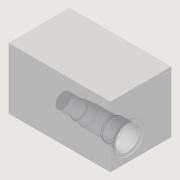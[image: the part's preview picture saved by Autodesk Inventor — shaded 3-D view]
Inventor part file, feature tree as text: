
AUTODESK INVENTOR PART (.ipt)
format: ipt  version: 2014 (Build 180170000, 170)  size: 204,800 bytes
history: native  units: mm
features: other x48, extrude x22, sketch x22
ambient origin geometry x8: Origin, YZ Plane, XZ Plane, XY Plane, X Axis, Y Axis, Z Axis, Center Point
bodies: 实体1 (feature_tree)
feature tree (92):
  extrude  "拉伸1"  Depth=30.2mm
  other  "UCS1"
  other  "UCS2"
  other  "UCS3"
  other  "UCS4"
  other  "UCS5"
  other  "UCS6"
  extrude  "拉伸2"  Depth=18.0mm
  extrude  "拉伸3"  Depth=0.79mm
  extrude  "拉伸5"  Depth=22.22mm
  extrude  "拉伸6"  Depth=14.28mm
  extrude  "拉伸7"  Depth=16.5mm TaperAngle=0.0deg
  extrude  "拉伸8"  Depth=38.5mm TaperAngle=0.0deg
  extrude  "拉伸9"  Depth=17.5mm
  extrude  "拉伸10"  Depth=47.63mm
  extrude  "拉伸11"  Depth=63.5mm TaperAngle=0.0deg
  extrude  "拉伸12"  Depth=63.5mm
  extrude  "拉伸13"  Depth=140.0mm
  extrude  "拉伸14"  Depth=0.79mm
  extrude  "拉伸15"  Depth=2.74mm
  extrude  "拉伸16"  Depth=12.7mm TaperAngle=0.0deg
  extrude  "拉伸17"  Depth=60.0mm TaperAngle=0.0deg
  extrude  "拉伸18"  Depth=60.0mm
  extrude  "拉伸19"  Depth=60.0mm
  extrude  "拉伸20"  Depth=60.0mm TaperAngle=0.0deg
  extrude  "拉伸21"  Depth=60.0mm
  extrude  "拉伸22"  Depth=60.0mm
  extrude  "拉伸23"  Depth=60.0mm TaperAngle=0.0deg
  sketch  "草图1"  dims[d0=60.0mm d1=0.0mm]
  sketch  "草图2"  dims[d2=0.0mm d3=0.0mm d4=0.0mm d5=0.0mm d6=0.0mm d7=0.0mm]
  sketch  "草图3"  dims[d8=0.0mm d9=0.0mm d10=0.0mm d11=0.0mm d12=0.0mm d13=0.0mm]
  sketch  "草图6"  dims[d14=0.0mm d15=0.0mm d16=0.0mm d17=0.0mm d18=0.0mm d19=0.0mm]
  sketch  "草图7"  dims[d20=0.0mm d21=0.0mm d22=0.0mm d23=0.0mm d24=0.0mm d25=0.0mm]
  sketch  "草图8"  dims[d26=0.0mm d27=0.0mm d28=0.0mm d29=0.0mm d30=0.0mm d31=0.0mm]
  sketch  "草图9"  dims[d32=0.0mm d33=0.0mm d34=0.0mm d35=0.0mm d36=0.0mm d37=0.0mm d38=30.2mm]
  sketch  "草图10"  dims[d39=20.0mm d40=18.0mm]
  sketch  "草图11"  dims[d41=0.79mm d42=0.0mm d43=24.0mm]
  sketch  "草图12"  dims[d44=2.74mm d45=-2.617994mm d49=22.22mm]
  sketch  "草图13"  dims[d50=14.28mm d51=0.0mm d52=14.28mm d53=-7.853982mm]
  sketch  "草图14"  dims[d54=20.63mm d55=16.5mm d56=0.0mm]
  sketch  "草图16"  dims[d57=19.08mm d58=38.5mm d59=0.0mm]
  sketch  "草图17"  dims[d60=38.5mm d61=-5.235988mm d62=17.5mm]
  sketch  "草图18"  dims[d63=47.63mm d64=0.0mm d65=47.63mm d66=-10.471976mm]
  sketch  "草图19"  dims[d67=15.0mm d68=63.5mm d69=0.0mm]
  sketch  "草图20"  dims[d70=63.5mm d71=-10.297443mm d75=30.2mm]
  sketch  "草图21"  dims[d76=80.0mm d77=140.0mm]
  sketch  "草图22"  dims[d78=0.79mm d79=0.0mm d80=20.7mm]
  sketch  "草图23"  dims[d81=2.74mm d82=-2.617994mm d83=2.74mm d84=-7.853982mm]
  sketch  "草图24"  dims[d85=19.05mm d86=12.7mm d87=0.0mm]
  sketch  "草图25"  dims[d88=17.48mm d89=19.05mm d90=0.0mm d91=19.05mm d92=-10.471976mm d93=12.7mm d94=29.3mm d95=0.0mm d96=29.3mm d97=-10.471976mm d98=11.0mm d99=38.1mm d100=0.0mm d101=38.1mm d102=-10.297443mm d106=100.0mm d107=60.0mm]
  other  "UCS1: YZ 平面"
  other  "UCS1: XZ 平面"
  other  "UCS1: XY 平面"
  other  "UCS1: X 轴"
  other  "UCS1: Y 轴"
  other  "UCS1: Z 轴"
  other  "UCS1: 原点"
  other  "UCS2: YZ 平面"
  other  "UCS2: XZ 平面"
  other  "UCS2: XY 平面"
  other  "UCS2: X 轴"
  other  "UCS2: Y 轴"
  other  "UCS2: Z 轴"
  other  "UCS2: 原点"
  other  "UCS3: YZ 平面"
  other  "UCS3: XZ 平面"
  other  "UCS3: XY 平面"
  other  "UCS3: X 轴"
  other  "UCS3: Y 轴"
  other  "UCS3: Z 轴"
  other  "UCS3: 原点"
  other  "UCS4: YZ 平面"
  other  "UCS4: XZ 平面"
  other  "UCS4: XY 平面"
  other  "UCS4: X 轴"
  other  "UCS4: Y 轴"
  other  "UCS4: Z 轴"
  other  "UCS4: 原点"
  other  "UCS5: YZ 平面"
  other  "UCS5: XZ 平面"
  other  "UCS5: XY 平面"
  other  "UCS5: X 轴"
  other  "UCS5: Y 轴"
  other  "UCS5: Z 轴"
  other  "UCS5: 原点"
  other  "UCS6: YZ 平面"
  other  "UCS6: XZ 平面"
  other  "UCS6: XY 平面"
  other  "UCS6: X 轴"
  other  "UCS6: Y 轴"
  other  "UCS6: Z 轴"
  other  "UCS6: 原点"
